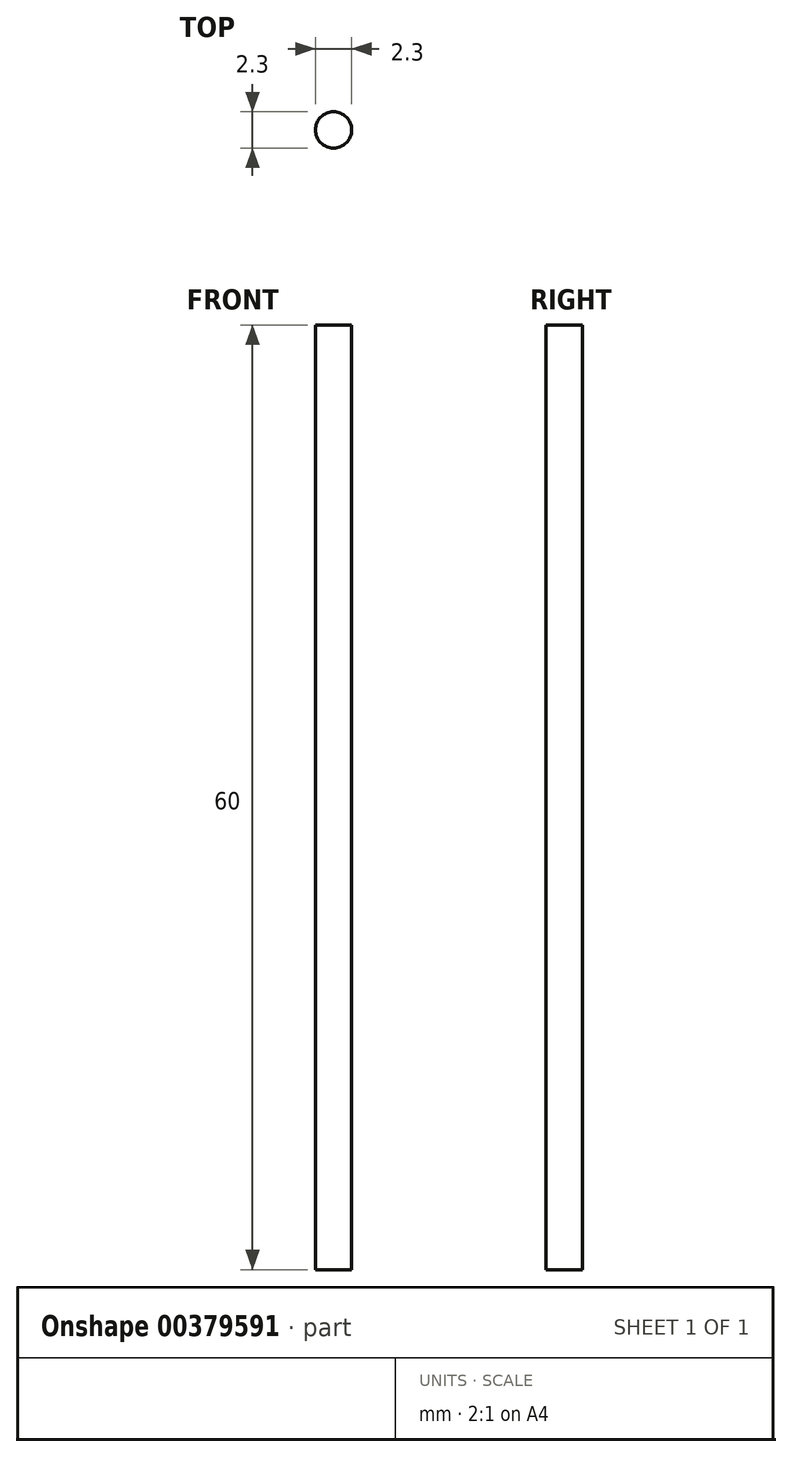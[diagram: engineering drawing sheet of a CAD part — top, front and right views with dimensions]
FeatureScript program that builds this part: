
annotation { "Feature Type Name" : "Feature", "Feature Type Description" : "" }
export const myFeature = defineFeature(function(context is Context, id is Id, definition is map)
    precondition{}
    {
        {
            var Q0;
            Q0=qCreatedBy(makeId("Top.planeOp"),FACE);
            var sketch = newSketch(context, id + "F0", { "sketchPlane" : qUnion([Q0])});
            skCircle(sketch, "E0", {"center": v(0, 0) * mm, "radius": 1.15 * mm});
            skSolve(sketch);
        }
        {
            var Q0;
            Q0 = qSketchRegion(id + "F0", true);
            extrude(context, id + "F1", {"entities" : qUnion([Q0]), "depth" : 60 * mm});
        }
    });
